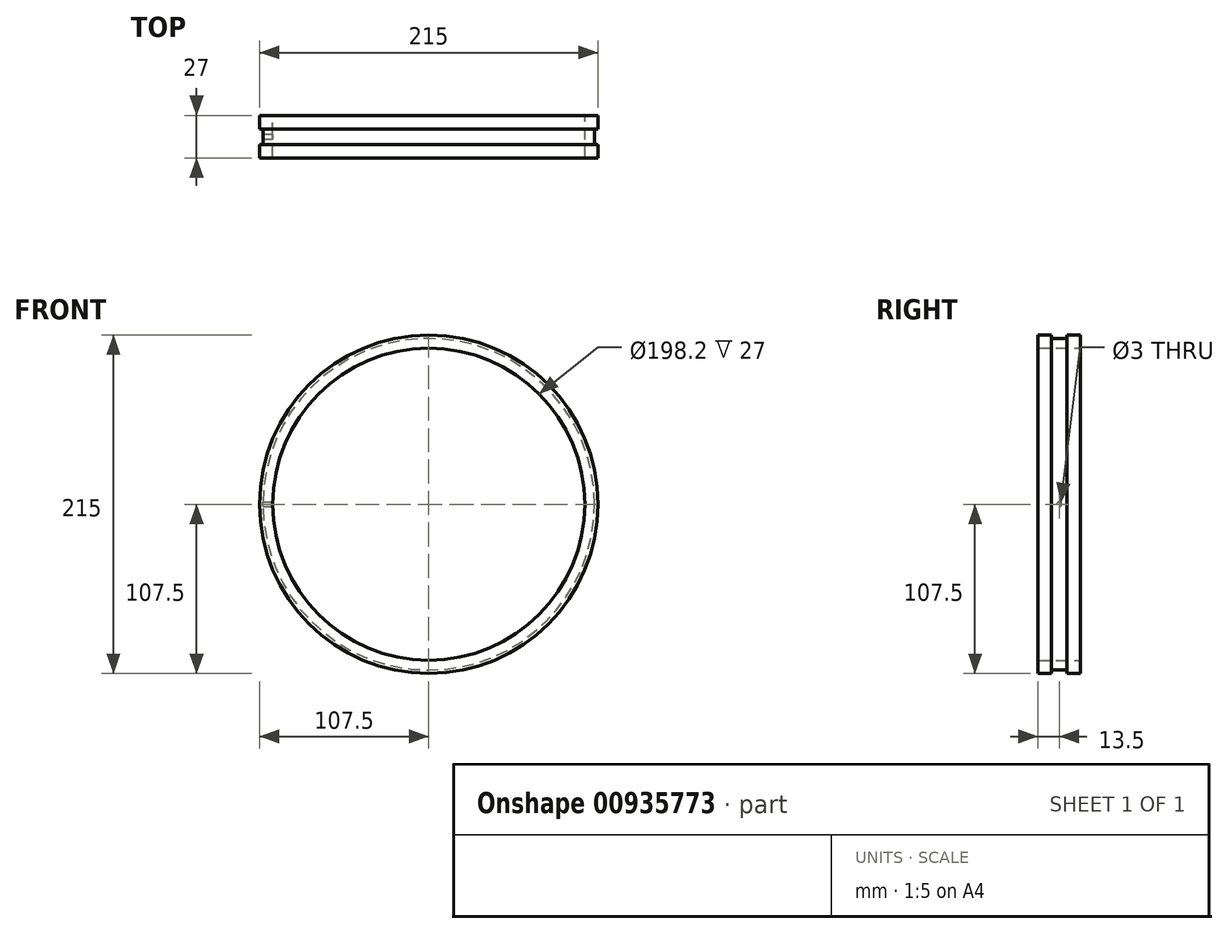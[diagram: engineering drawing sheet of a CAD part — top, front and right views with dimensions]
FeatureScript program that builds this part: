
annotation { "Feature Type Name" : "Feature", "Feature Type Description" : "" }
export const myFeature = defineFeature(function(context is Context, id is Id, definition is map)
    precondition{}
    {
        {
            var Q0;
            Q0=qCreatedBy(makeId("Front.planeOp"),FACE);
            var sketch = newSketch(context, id + "F0", { "sketchPlane" : qUnion([Q0])});
            skCircle(sketch, "E0", {"center": v(0, 0) * mm, "radius": 107.5 * mm});
            skCircle(sketch, "E1", {"center": v(0, 0) * mm, "radius": 99.1 * mm});
            skCircle(sketch, "E2", {"center": v(0, 0) * mm, "radius": 1.5 * mm});
            skSolve(sketch);
        }
        {
            var Q0;
            Q0=makeQuery(id+"F0.imprint","IMPRINT",FACE,{"disambiguationData":[TD([[makeQuery(id+"F0.imprint","IMPRINT",EDGE,{"derivedFrom":sQuery(id+"F0.wireOp",EDGE,"E0")}),1.0]])]});
            extrude(context, id + "F1", {"entities" : qUnion([Q0]), "depth" : 27 * mm, "offsetDistance" : 25 * mm});
        }
        {
            var Q0;
            Q0=qCreatedBy(makeId("Top.planeOp"),FACE);
            var sketch = newSketch(context, id + "F2", { "sketchPlane" : qUnion([Q0])});
            skLineSegment(sketch, "E3", {"start": v(105.3, -18.4) * mm, "end": v(105.3, -8.6) * mm});
            skLineSegment(sketch, "E4", {"start": v(105.3, -8.6) * mm, "end": v(128.38, -8.6) * mm});
            skLineSegment(sketch, "E5", {"start": v(128.38, -8.6) * mm, "end": v(128.38, -18.4) * mm});
            skLineSegment(sketch, "E6", {"start": v(105.3, -18.4) * mm, "end": v(128.38, -18.4) * mm});
            skSolve(sketch);
        }
        {
            var Q0;
            Q0=makeQuery(id+"F2.imprint","IMPRINT",FACE,{"disambiguationData":[TD([[makeQuery(id+"F2.imprint","IMPRINT",EDGE,{"derivedFrom":sQuery(id+"F2.wireOp",EDGE,"E3")}),-1.0]])]});
            var Q1;
            Q1=sQuery(id+"F2.wireOp",EDGE,"E4");
            var Q2;
            Q2=sQuery(id+"F2.wireOp",EDGE,"E3");
            var Q3;
            Q3=sQuery(id+"F2.wireOp",EDGE,"E5");
            var Q4;
            Q4=sQuery(id+"F2.wireOp",EDGE,"K219f0If-lrTU-LQaM-gwQl-uJoxXXmMJM0X.bottom");
            var Q5;
            Q5=makeQuery(id+"F1.opExtrude","CAP_EDGE",EDGE,{"disambiguationData":[OSD([sQuery(id+"F0.wireOp",EDGE,"E0")])],"isStart":false});
            sweep(context, id + "F3", {"operationType" : NewBodyOperationType.REMOVE, "profiles" : qUnion([Q0]), "surfaceProfiles" : qUnion([Q1, Q2, Q3, Q4]), "path" : qUnion([Q5])});
        }
        {
            var Q0;
            Q0=qCreatedBy(makeId("Right.planeOp"),FACE);
            var sketch = newSketch(context, id + "F4", { "sketchPlane" : qUnion([Q0])});
            skCircle(sketch, "E7", {"center": v(-13.5, 0) * mm, "radius": 1.5 * mm});
            skSolve(sketch);
        }
        {
            var Q0;
            Q0 = qSketchRegion(id + "F4", true);
            extrude(context, id + "F5", {"entities" : qUnion([Q0]), "operationType" : NewBodyOperationType.REMOVE, "oppositeDirection" : true, "depth" : 124.5 * mm, "offsetDistance" : 25 * mm});
        }
    });
